# Revit family: CADS_AIRFLOWdev_AirflexPro_Oval_WallFloorCeilingOutlet_Supply
name_source: partatom
category: Duct Fittings
revit_build: Autodesk Revit 2015 (Build: 20160512_1515(x64)
units: mm (PartAtom-declared; Revit-internal decimal feet)

## types (1)
- CADS_AIRFLOWdev_AirflexPro_Oval_WallFloorCeilingOutlet_Supply
    6MonthlyMaintenance = Visually inspect system, clean the fan and ducting if necessary
    AssemblyPlace = UNKNOWN
    AssetType = FIXED
    Body = CADS_AIRFLOWdev_SteelGalvanized
    CADS_Index = 0
    CEApproval = Yes
    Color = Grey
    Constituents = 90° Wall/Floor/Ceiling Outlet-Oval
    DurationUnit = Year
    ExpectedServiceLife = 10
    Features = 90° Wall/Floor/Ceiling Outlet-Oval
    Finish = Lacquer
    FireControlPanelLinks = No
    Fitting Type = Ignore
    Grade = Virgin
    GrossWeight = 1.57 kg
    Halfb1 = 160 mm  [stored 0.524934 ft]
    ISO140001 = Yes
    ISO90001 = Yes
    IsExtendedWarranty = No
    Manufacturer = Airflow Developments Ltd
    ManufacturerAddress = Aidelle House
Lancaster Road
Cressex Business Park
High Wycombe
Bucks
HP123QP
    ManufacturerTelephone = 01494 525252
    ManufacturerWebsite = www.airflow.com
    Material = Plastic
    NBSCode = 45-80-50/394 Ventilation ducts
    NominalHeight = 180 mm
    NominalLength = 300 mm
    NominalWidth = 335 mm
    PassiveHouseApproval = No
    PointOfContact = Airflow Developments Ltd
    ProductLiterature = https://www.airflow.com
    ProductionYear = 2017
    Quantity = 1
    RedDotDesignAward = No
    ReplacementCost = 107.46
    SAPApproval = Yes
    ServiceLifeDuration = 10
    ServiceLifeType = EXPECTEDSERVICELIFE
    Shape = Other
    ShippingWeight = 1.89 kg
    Size = 300 x 335 x 180
    Status = New
    TemperatureRange = up to 40°C
    Uniclass2015 = Pr_30_59_96_92:Ventilation ducts
    WarrantyGuarantor = Airflow Developments Ltd
    WarrantyPeriod = 0
    b1 = 319 mm  [stored 1.04659 ft]
    h1 = 121 mm  [stored 0.396982 ft]
    l1 = 220 mm  [stored 0.721785 ft]

note: [stored X ft] marks values corroborated as IEEE doubles in the binary element streams (Revit-internal decimal feet)

## geometry (parser evidence)
native form markers: Blend x12, Sweep x41
no freeform markers — native parametric forms only
